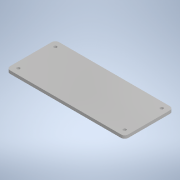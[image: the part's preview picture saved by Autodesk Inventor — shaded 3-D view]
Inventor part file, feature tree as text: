
AUTODESK INVENTOR PART (.ipt)
format: ipt  version: 2022.1 (Build 261234020, 234B)  size: 169,472 bytes
history: native  units: in
note: dims shown in document units (in); Inventor stores cm internally (conversion verified against a paired STEP export)
features: extrude x1, sketch x1, other x1
ambient origin geometry x8: Origin, YZ Plane, XZ Plane, XY Plane, X Axis, Y Axis, Z Axis, Center Point
bodies: Solido1 (feature_tree)
feature tree (3):
  extrude  "Estrusione1"  Depth=0.3937in TaperAngle=0.0deg
  sketch  "Schizzo1"
  other  "buttonpad"
